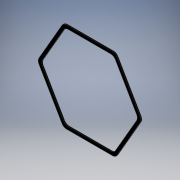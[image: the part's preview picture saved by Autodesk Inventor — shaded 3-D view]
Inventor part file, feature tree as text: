
AUTODESK INVENTOR PART (.ipt)
format: ipt  version: 2019 (Build 230136000, 136)  size: 140,288 bytes
history: native  units: mm
features: extrude x2, fillet x2, sketch x2, projected_geometry x1
ambient origin geometry x8: Origin, YZ Plane, XZ Plane, XY Plane, X Axis, Y Axis, Z Axis, Center Point
bodies: Solid1 (feature_tree)
feature tree (7):
  extrude  "Extrusion1"  Depth=2.0mm TaperAngle=0.0deg
  extrude  "Extrusion6"  Depth=10.0mm
  fillet  "Fillet2"  Radius=10.0mm
  fillet  "Fillet3"  Radius=6.0mm
  sketch  "Sketch1"  dims[d0=175.0mm d1=2.0mm d2=0.0mm]
  sketch  "Sketch7"  dims[d20=7.0mm d21=0.0mm d24=10.0mm d25=10.0mm d26=6.0mm]
  projected_geometry  "Projected Loop7"
